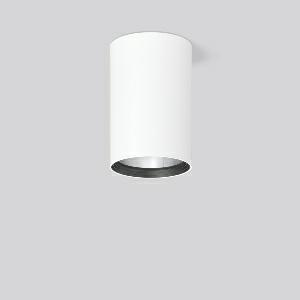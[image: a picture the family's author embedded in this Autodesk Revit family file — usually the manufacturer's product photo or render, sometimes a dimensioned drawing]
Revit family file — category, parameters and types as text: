
# Revit family: heledon_maxi_a_931225_002_3_b62d
name_source: partatom
category: Lighting Fixtures
units: mm (PartAtom-declared; Revit-internal decimal feet)

## family parameters
Cut with Voids When Loaded = No
Host = Face
Light Source = No
Part Type = Normal
Room Calculation Point = No
Round Connector Dimension = Use Diameter
Shared = No

## types (1)
- HELEDON maxi A (1 x LED Modul 935, 4400 lm, 3500)
    Apparent Load = 35 VA
    Approval mark = CE
    CIE Flux Codes = 100 100 100 100 100
    Color Rendering = 92
    Color Temperature = 3500
    Default Elevation = 1800 mm
    Description = Series: HELEDON maxi
Cylindrical surface-mounted downlight. Housing: die-cast aluminium, powder-coated. Internal ceiling frame polycarbonate with bayonet mounting. Black plastic ring and recessed LED to prevent glare from the side. Optical assembly with reflector made of MIRO-Silver with 98% total light reflection for outstanding efficiency - can be changed without tools. Best colour rendering index Ra>90. Suitable for Ceiling mounting. Easy installation with a separate ceiling frame with bayonet mounting and plug connection. Driver integrated. Connected via plug-in connector. High quality converter without flickering and stroboscopic effect. The following accessories can be mounted without use of tools: interchangeable lenses, decorative glasses, honeycomb louvre, clear and frosted diffusers, white interchangeable plastic ring. 
Colour: traffic white, matt (RAL 9016)
Diameter: 123 mm
Height: 183 mm
Lamp: LED
Socket: without socket
Colour temperature: 3500K
Colour rendering index (CRI): 92
System power: 35 W
Rated luminous flux: 4400 lm
Luminous efficiency: 126 lm/W
Control gear: Regulated power supply
Protection class: I
Type of protection: IP 20
    Height = 183 mm
    Lamp = 1 x LED Modul 935
    Lamp Light Flux = 4400 lm
    Lamp count = 1
    Length = 123 mm
    Lifetime = 50000 h
    Luminous efficacy = 126 lm/W
    Manufacturer = RZB
    ModVariant = No
    Model = 931225.002.3
    Mounting Place = Ceiling
    Mounting Type = Surface mounted
    Number of Poles = 1
    OnlyDefault = Yes
    Power Factor = 1
    Product Name = HELEDON maxi A
    Product group = Surface mounted downlights
    ProductGroupID = 302
    Protection Class = Protection class I
    Protection Degree = IP 20
    RLX_Detail_Level = 1
    RLX_Emergency_Light_Flux = 0 lm
    RLX_Emergency_Type = 0
    RLX_Emergency_Type_DB = No
    RlxData = <blob elided: 97089 chars, md5=582bd756>
    Socket = socket
    Standby Power = 0 W
    System Light Flux = 4400 lm
    System Power = 35 W
    Type Comments = Product without accessories
    Type Image = 931192.002.jpg
    URL = http://relux.com
    VarID = ---
    Voltage = 230 V
    Voltage Range = 220-240 V
    Weight = 0.00 kg
    Width = 0 mm  [stored 0 ft]

note: [stored X ft] marks values corroborated as IEEE doubles in the binary element streams (Revit-internal decimal feet)

## geometry (parser evidence)
native form markers: Blend x4, Sweep x9
no freeform markers — native parametric forms only
